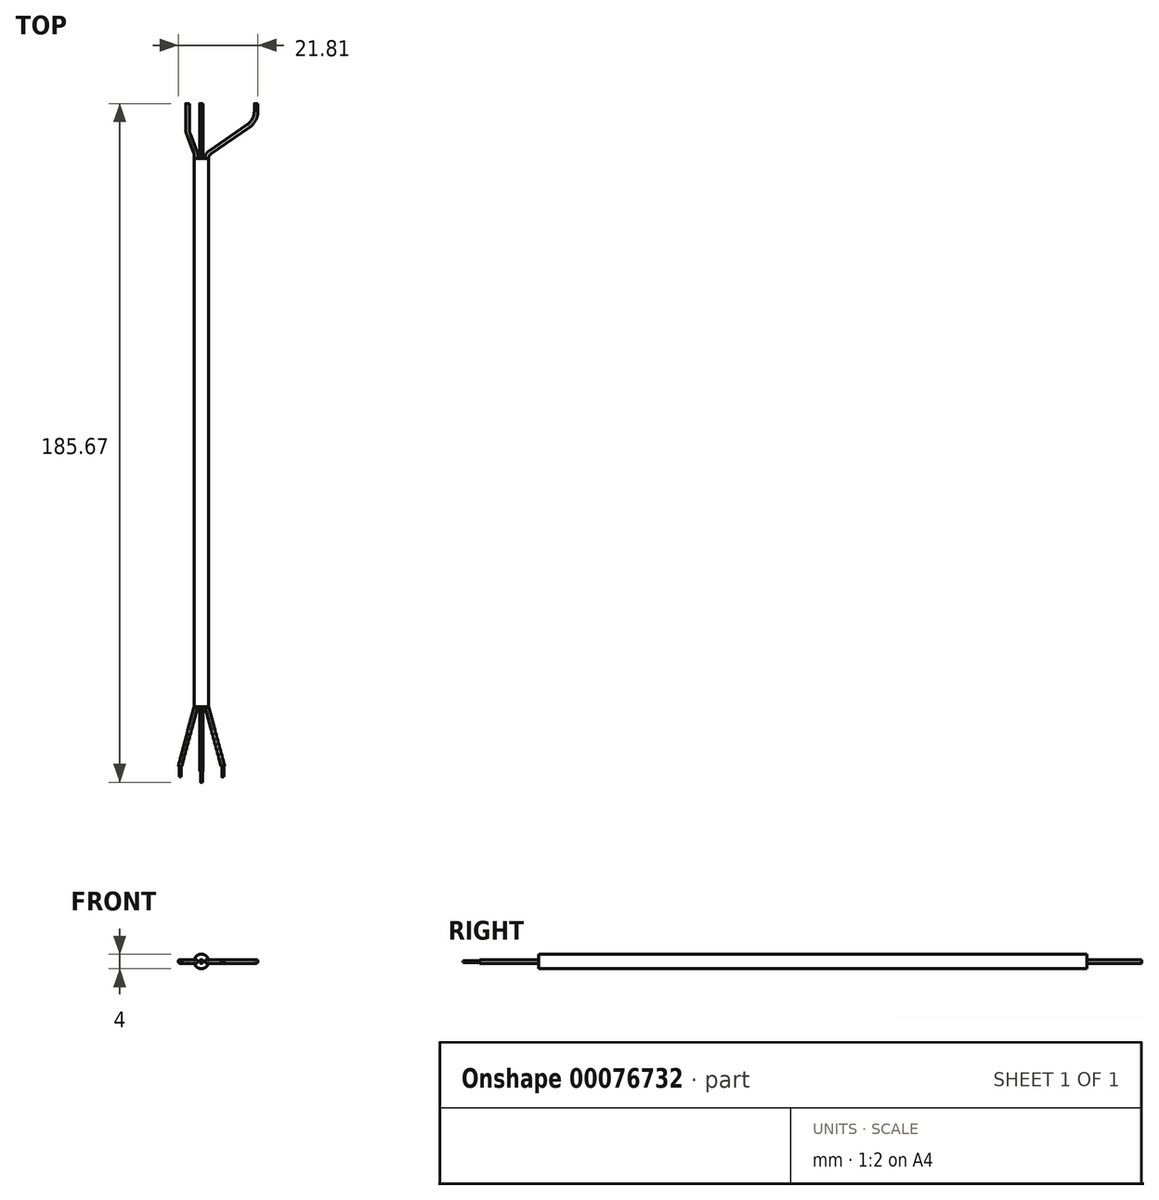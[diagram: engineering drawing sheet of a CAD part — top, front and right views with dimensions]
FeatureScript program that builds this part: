
annotation { "Feature Type Name" : "Feature", "Feature Type Description" : "" }
export const myFeature = defineFeature(function(context is Context, id is Id, definition is map)
    precondition{}
    {
        {
            var Q0;
            Q0=qCreatedBy(makeId("Front.planeOp"),FACE);
            var sketch = newSketch(context, id + "F0", { "sketchPlane" : qUnion([Q0])});
            skCircle(sketch, "E0", {"center": v(0, 0) * mm, "radius": 2 * mm});
            skSolve(sketch);
        }
        {
            var Q0;
            Q0=qSketchRegion(id+"F0",true);
            extrude(context, id + "F1", {"entities" : qUnion([Q0]), "depth" : 150 * mm, "symmetric" : true});
        }
        {
            var Q0;
            Q0=qCreatedBy(makeId("Top.planeOp"),FACE);
            var sketch = newSketch(context, id + "F2", { "sketchPlane" : qUnion([Q0])});
            skLineSegment(sketch, "E1", {"start": v(0, 75) * mm, "end": v(0, 90) * mm});
            skLineSegment(sketch, "E2", {"start": v(-1.5, 75) * mm, "end": v(-1.5, 76) * mm});
            skLineSegment(sketch, "E3", {"start": v(-1.64, 76.73) * mm, "end": v(-3.46, 81.39) * mm});
            skLineSegment(sketch, "E4", {"start": v(-3.81, 83.21) * mm, "end": v(-3.81, 90) * mm});
            skLineSegment(sketch, "E5", {"start": v(2.36, 76.65) * mm, "end": v(12.84, 83.89) * mm});
            skLineSegment(sketch, "E6", {"start": v(15, 88) * mm, "end": v(15, 90) * mm});
            skPoint(sketch, "E7.visualSharp", {"position": v(1.98, 76.38) * mm});
            skArc(sketch, "E7.filletArc", {"start": v(2.36, 76.65) * mm, "mid": v(1.73, 75.93) * mm, "end": v(1.5, 75) * mm});
            skPoint(sketch, "E8.visualSharp", {"position": v(-1.5, 76.38) * mm});
            skArc(sketch, "E8.filletArc", {"start": v(-1.5, 76) * mm, "mid": v(-1.53, 76.37) * mm, "end": v(-1.64, 76.73) * mm});
            skPoint(sketch, "E9.visualSharp", {"position": v(15, 85.38) * mm});
            skArc(sketch, "E9.filletArc", {"start": v(12.84, 83.89) * mm, "mid": v(14.43, 85.68) * mm, "end": v(15, 88) * mm});
            skPoint(sketch, "E10.visualSharp", {"position": v(-3.8, 82.27) * mm});
            skArc(sketch, "E10.filletArc", {"start": v(-3.8, 83.21) * mm, "mid": v(-3.72, 82.28) * mm, "end": v(-3.46, 81.39) * mm});
            skLineSegment(sketch, "E11", {"start": v(1.5, 75) * mm, "end": v(1.5, 78.9) * mm, "construction": true});
            skSolve(sketch);
        }
        {
            var Q0;
            Q0=qCreatedBy(makeId("Top.planeOp"),FACE);
            var sketch = newSketch(context, id + "F3", { "sketchPlane" : qUnion([Q0])});
            skLineSegment(sketch, "E12", {"start": v(0, -75) * mm, "end": v(0, -92.67) * mm});
            skLineSegment(sketch, "E13", {"start": v(1.5, -75) * mm, "end": v(5.84, -91.2) * mm});
            skLineSegment(sketch, "E14", {"start": v(-1.5, -75) * mm, "end": v(-5.84, -91.2) * mm});
            skSolve(sketch);
        }
        {
            var Q0;
            Q0=makeQuery(id+"F1.opExtrude","CAP_FACE",FACE,{"disambiguationData":[OSD([sQuery(id+"F0.wireOp",EDGE,"E0")])],"isStart":true});
            var sketch = newSketch(context, id + "F4", { "sketchPlane" : qUnion([Q0])});
            skCircle(sketch, "E15", {"center": v(1.5, 0) * mm, "radius": 0.5 * mm});
            skSolve(sketch);
        }
        {
            var Q0;
            Q0=makeQuery(id+"F4.imprint","IMPRINT",FACE,{"disambiguationData":[TD([[makeQuery(id+"F4.imprint","IMPRINT",EDGE,{"derivedFrom":sQuery(id+"F4.wireOp",EDGE,"E15")}),1.0]])]});
            var Q1;
            Q1=sQuery(id+"F2.wireOp",EDGE,"E2");
            var Q2;
            Q2=sQuery(id+"F2.wireOp",EDGE,"E8.filletArc");
            var Q3;
            Q3=sQuery(id+"F2.wireOp",EDGE,"E3");
            var Q4;
            Q4=sQuery(id+"F2.wireOp",EDGE,"E10.filletArc");
            var Q5;
            Q5=sQuery(id+"F2.wireOp",EDGE,"E4");
            sweep(context, id + "F5", {"profiles" : qUnion([Q0]), "path" : qUnion([Q1, Q2, Q3, Q4, Q5])});
        }
        {
            var Q0;
            Q0=makeQuery(id+"F1.opExtrude","CAP_FACE",FACE,{"disambiguationData":[OSD([sQuery(id+"F0.wireOp",EDGE,"E0")])],"isStart":true});
            var sketch = newSketch(context, id + "F6", { "sketchPlane" : qUnion([Q0])});
            skCircle(sketch, "E16", {"center": v(0, 0) * mm, "radius": 0.5 * mm});
            skSolve(sketch);
        }
        {
            var Q0;
            Q0=makeQuery(id+"F6.imprint","IMPRINT",FACE,{"disambiguationData":[TD([[makeQuery(id+"F6.imprint","IMPRINT",EDGE,{"derivedFrom":sQuery(id+"F6.wireOp",EDGE,"E16")}),1.0]])]});
            var Q1;
            Q1=sQuery(id+"F2.wireOp",EDGE,"E1");
            sweep(context, id + "F7", {"profiles" : qUnion([Q0]), "path" : qUnion([Q1])});
        }
        {
            var Q0;
            Q0=makeQuery(id+"F1.opExtrude","CAP_FACE",FACE,{"disambiguationData":[OSD([sQuery(id+"F0.wireOp",EDGE,"E0")])],"isStart":true});
            var sketch = newSketch(context, id + "F8", { "sketchPlane" : qUnion([Q0])});
            skCircle(sketch, "E17", {"center": v(-1.47, 0) * mm, "radius": 0.5 * mm});
            skSolve(sketch);
        }
        {
            var Q0;
            Q0=makeQuery(id+"F8.imprint","IMPRINT",FACE,{"disambiguationData":[TD([[makeQuery(id+"F8.imprint","IMPRINT",EDGE,{"derivedFrom":sQuery(id+"F8.wireOp",EDGE,"E17")}),1.0]])]});
            var Q1;
            Q1=sQuery(id+"F2.wireOp",EDGE,"ZGmxyzHz-ZjXG-v1H0-Yx3K-jGNV5d4o1gtK");
            var Q2;
            Q2=sQuery(id+"F2.wireOp",EDGE,"E7.filletArc");
            var Q3;
            Q3=sQuery(id+"F2.wireOp",EDGE,"E5");
            var Q4;
            Q4=sQuery(id+"F2.wireOp",EDGE,"E9.filletArc");
            var Q5;
            Q5=sQuery(id+"F2.wireOp",EDGE,"E6");
            sweep(context, id + "F9", {"profiles" : qUnion([Q0]), "path" : qUnion([Q1, Q2, Q3, Q4, Q5])});
        }
        {
            var Q0;
            Q0=makeQuery(id+"F1.opExtrude","CAP_FACE",FACE,{"disambiguationData":[OSD([sQuery(id+"F0.wireOp",EDGE,"E0")])],"isStart":false});
            var sketch = newSketch(context, id + "F10", { "sketchPlane" : qUnion([Q0])});
            skCircle(sketch, "E18", {"center": v(0, 0) * mm, "radius": 0.5 * mm});
            skCircle(sketch, "E19", {"center": v(-1.5, 0) * mm, "radius": 0.5 * mm});
            skCircle(sketch, "E20", {"center": v(1.5, 0) * mm, "radius": 0.5 * mm});
            skSolve(sketch);
        }
        {
            var Q0;
            Q0=makeQuery(id+"F10.imprint","IMPRINT",FACE,{"disambiguationData":[TD([[makeQuery(id+"F10.imprint","IMPRINT",EDGE,{"derivedFrom":sQuery(id+"F10.wireOp",EDGE,"E18")}),1.0]])]});
            var Q1;
            Q1=sQuery(id+"F3.wireOp",EDGE,"E12");
            sweep(context, id + "F11", {"profiles" : qUnion([Q0]), "path" : qUnion([Q1])});
        }
        {
            var Q0;
            Q0=makeQuery(id+"F10.imprint","IMPRINT",FACE,{"disambiguationData":[TD([[makeQuery(id+"F10.imprint","IMPRINT",EDGE,{"derivedFrom":sQuery(id+"F10.wireOp",EDGE,"E19")}),1.0]])]});
            var Q1;
            Q1=sQuery(id+"F3.wireOp",EDGE,"E14");
            sweep(context, id + "F12", {"profiles" : qUnion([Q0]), "path" : qUnion([Q1])});
        }
        {
            var Q0;
            Q0=makeQuery(id+"F10.imprint","IMPRINT",FACE,{"disambiguationData":[TD([[makeQuery(id+"F10.imprint","IMPRINT",EDGE,{"derivedFrom":sQuery(id+"F10.wireOp",EDGE,"E20")}),1.0]])]});
            var Q1;
            Q1=sQuery(id+"F3.wireOp",EDGE,"E13");
            sweep(context, id + "F13", {"profiles" : qUnion([Q0]), "path" : qUnion([Q1])});
        }
        {
            var Q0;
            Q0=makeQuery(id+"F13.opSweep","CAP_FACE",FACE,{"disambiguationData":[OSD([sQuery(id+"F3.wireOp",VERTEX,"E13.end"),sQuery(id+"F10.wireOp",EDGE,"E20")])],"isStart":false});
            var sketch = newSketch(context, id + "F14", { "sketchPlane" : qUnion([Q0])});
            skCircle(sketch, "E21", {"center": v(5.84, 0) * mm, "radius": 0.25 * mm});
            skCircle(sketch, "E22", {"center": v(-5.84, 0) * mm, "radius": 0.25 * mm});
            skSolve(sketch);
        }
        {
            var Q0;
            Q0=qSketchRegion(id+"F14",true);
            extrude(context, id + "F15", {"entities" : qUnion([Q0]), "depth" : 3 * mm});
        }
        {
            var Q0;
            Q0=makeQuery(id+"F11.opSweep","CAP_FACE",FACE,{"disambiguationData":[OSD([sQuery(id+"F3.wireOp",VERTEX,"E12.end"),sQuery(id+"F10.wireOp",EDGE,"E18")])],"isStart":false});
            var sketch = newSketch(context, id + "F16", { "sketchPlane" : qUnion([Q0])});
            skCircle(sketch, "E23", {"center": v(0, 0) * mm, "radius": 0.25 * mm});
            skSolve(sketch);
        }
        {
            var Q0;
            Q0=qSketchRegion(id+"F16",true);
            extrude(context, id + "F17", {"entities" : qUnion([Q0]), "depth" : 3 * mm});
        }
    });
